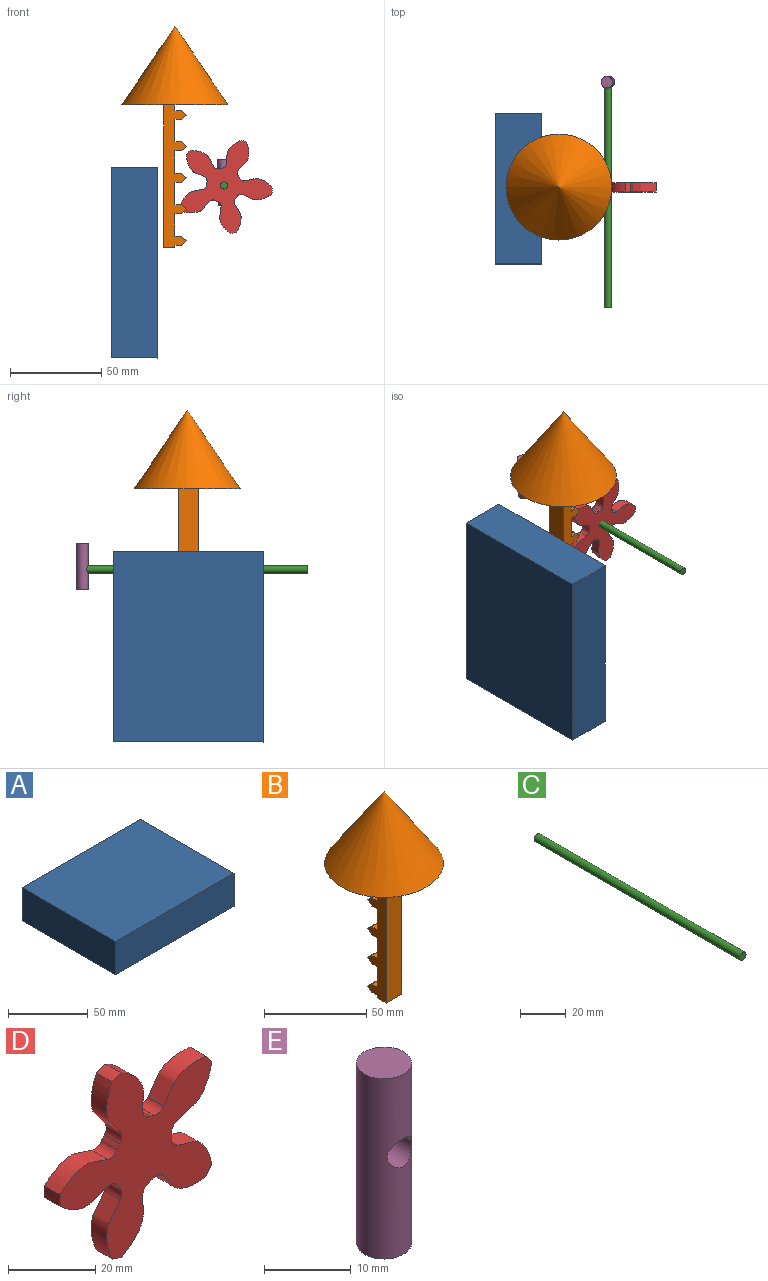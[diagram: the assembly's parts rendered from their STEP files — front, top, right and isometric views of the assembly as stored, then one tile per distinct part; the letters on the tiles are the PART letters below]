
ASSEMBLY  parts=5 mates=3
PART A: 6 faces, bbox 104.7x82.7x25.4 mm
  f0: plane 104.67x25.4mm, normal (0,1,0), area 2658.7mm2, adj f1,f3,f4,f5
  f1: plane 82.72x25.4mm, normal (-1,0,0), area 2101mm2, adj f0,f2,f4,f5
  f2: plane 104.67x25.4mm, normal (0,-1,0), area 2658.7mm2, adj f1,f3,f4,f5
  f3: plane 82.72x25.4mm, normal (1,0,0), area 2101mm2, adj f0,f2,f4,f5
  f4: plane 104.67x82.72mm, normal (0,0,1), area 8658.4mm2, adj f0,f1,f2,f3
  f5: plane 104.67x82.72mm, normal (0,0,-1), area 8658.4mm2, adj f0,f1,f2,f3
PART B: 32 faces, bbox 58.2x58.2x121.8 mm
  f0: plane 78.49x10.66mm, normal (0,-1,0), area 836.5mm2, adj f27,f28,f30,f31
  f1: plane 10.66x3.11mm, normal (0,1,0), area 33.1mm2, adj f26,f28,f30,f31
  f2: plane 10.66x1.43mm, normal (0,1,0), area 15.3mm2, adj f13,f27,f30,f31
  f3: plane 10.66x2.79mm, normal (0,0.64,-0.76), area 38.9mm2, adj f4,f13,f30,f31
  f4: plane 10.66x2.79mm, normal (0,0.67,0.74), area 39.9mm2, adj f3,f14,f30,f31
  f5: plane 10.66x2.79mm, normal (0,0.64,-0.76), area 38.9mm2, adj f6,f16,f30,f31
  f6: plane 10.66x2.79mm, normal (0,0.67,0.74), area 39.9mm2, adj f5,f17,f30,f31
  f7: plane 10.66x2.79mm, normal (0,0.64,-0.76), area 38.9mm2, adj f8,f19,f30,f31
  f8: plane 10.66x2.79mm, normal (0,0.67,0.74), area 39.9mm2, adj f7,f20,f30,f31
  f9: plane 10.66x2.79mm, normal (0,0.64,-0.76), area 38.9mm2, adj f10,f22,f30,f31
  f10: plane 10.66x2.79mm, normal (0,0.67,0.74), area 39.9mm2, adj f9,f23,f30,f31
  f11: plane 10.66x2.79mm, normal (0,0.64,-0.76), area 38.9mm2, adj f12,f25,f30,f31
  f12: plane 10.66x2.79mm, normal (0,0.67,0.74), area 39.9mm2, adj f11,f26,f30,f31
  f13: plane 10.66x3.77mm, normal (0,0,-1), area 40.2mm2, adj f2,f3,f30,f31
  f14: plane 10.66x3.77mm, normal (0,0,1), area 40.2mm2, adj f4,f15,f30,f31
  f15: plane 12.42x10.66mm, normal (0,1,0), area 132.3mm2, adj f14,f16,f30,f31
  f16: plane 10.66x3.77mm, normal (0,0,-1), area 40.2mm2, adj f5,f15,f30,f31
  f17: plane 10.66x3.77mm, normal (0,0,1), area 40.2mm2, adj f6,f18,f30,f31
  f18: plane 12.42x10.66mm, normal (0,1,0), area 132.3mm2, adj f17,f19,f30,f31
  f19: plane 10.66x3.77mm, normal (0,0,-1), area 40.2mm2, adj f7,f18,f30,f31
  f20: plane 10.66x3.77mm, normal (0,0,1), area 40.2mm2, adj f8,f21,f30,f31
  f21: plane 12.42x10.66mm, normal (0,1,0), area 132.3mm2, adj f20,f22,f30,f31
  f22: plane 10.66x3.77mm, normal (0,0,-1), area 40.2mm2, adj f9,f21,f30,f31
  f23: plane 10.66x3.77mm, normal (0,0,1), area 40.2mm2, adj f10,f24,f30,f31
  f24: plane 12.42x10.66mm, normal (0,1,0), area 132.3mm2, adj f23,f25,f30,f31
  f25: plane 10.66x3.77mm, normal (0,0,-1), area 40.2mm2, adj f11,f24,f30,f31
  f26: plane 10.66x3.77mm, normal (0,0,1), area 40.2mm2, adj f1,f12,f30,f31
  f27: plane 10.66x6.14mm, normal (0,0,-1), area 65.5mm2, adj f0,f2,f30,f31
  f28: plane 58.19x58.19mm, normal (0,0,-1), area 2594.1mm2, adj f0,f1,f29,f30,f31
  f29: cone r=29.1mm half-angle=33.9deg, axis (0,0,-1), area 4770.6mm2, adj f28
  f30: plane 78.49x12.7mm, normal (1,0,0), area 607.4mm2, adj f0,f1,f2,f3,f4,f5,f6,f7
  f31: plane 78.49x12.7mm, normal (-1,0,0), area 607.4mm2, adj f0,f1,f2,f3,f4,f5,f6,f7
PART C: 3 faces, bbox 4x127x4 mm
  f0: cylinder r=1.99mm len=127mm, axis (0,1,0), area 1585.8mm2, adj f1,f2
  f1: plane 3.97x3.97mm, normal (0,-1,0), area 12.4mm2, adj f0
  f2: plane 3.97x3.97mm, normal (0,1,0), area 12.4mm2, adj f0
PART D: 32 faces, bbox 49.5x5.1x52.1 mm
  f0: cylinder r=26.67mm len=5.08mm, axis (0,1,0), area 16.2mm2, adj f4,f6,f12,f29
  f1: cylinder r=26.67mm len=5.08mm, axis (0,1,0), area 16.2mm2, adj f4,f6,f24,f27
  f2: cylinder r=26.67mm len=5.08mm, axis (0,1,0), area 16.2mm2, adj f4,f6,f7,f19
  f3: cylinder r=26.67mm len=5.08mm, axis (0,1,0), area 16.2mm2, adj f4,f6,f14,f17
  f4: plane 52.12x49.47mm, normal (0,-1,0), area 1078.2mm2, adj f0,f1,f2,f3,f5,f7,f8,f9
  f5: cylinder r=26.67mm len=5.08mm, axis (0,1,0), area 16.2mm2, adj f4,f6,f9,f22
  f6: plane 52.12x49.47mm, normal (0,1,0), area 1078.2mm2, adj f0,f1,f2,f3,f5,f7,f8,f9
  f7: extruded ~11.11x10.86mm, area 85.6mm2, adj f2,f4,f6,f10
  f8: cylinder r=9.53mm len=5.08mm, axis (0,1,0), area 7.7mm2, adj f4,f6,f10,f11
  f9: extruded ~11.11x10.86mm, area 85.6mm2, adj f4,f5,f6,f11
  f10: cylinder r=2.65mm len=5.08mm, axis (0,1,0), area 18.2mm2, adj f4,f6,f7,f8
  f11: cylinder r=2.65mm len=5.08mm, axis (0,1,0), area 18.2mm2, adj f4,f6,f8,f9
  f12: extruded ~15.38x5.08mm, area 85.6mm2, adj f0,f4,f6,f15
  f13: cylinder r=9.53mm len=5.08mm, axis (0,1,0), area 7.7mm2, adj f4,f6,f15,f16
  f14: extruded ~15.32x5.08mm, area 85.6mm2, adj f3,f4,f6,f16
  f15: cylinder r=2.65mm len=5.08mm, axis (0,1,0), area 18.2mm2, adj f4,f6,f12,f13
  f16: cylinder r=2.65mm len=5.08mm, axis (0,1,0), area 18.2mm2, adj f4,f6,f13,f14
  f17: extruded ~13.93x6.98mm, area 85.6mm2, adj f3,f4,f6,f20
  f18: cylinder r=9.53mm len=5.08mm, axis (0,1,0), area 7.7mm2, adj f4,f6,f20,f21
  f19: extruded ~13.77x7.42mm, area 85.6mm2, adj f2,f4,f6,f21
  f20: cylinder r=2.65mm len=5.08mm, axis (0,1,0), area 18.2mm2, adj f4,f6,f17,f18
  f21: cylinder r=2.65mm len=5.08mm, axis (0,1,0), area 18.2mm2, adj f4,f6,f18,f19
  f22: extruded ~13.77x7.42mm, area 85.6mm2, adj f4,f5,f6,f25
  f23: cylinder r=9.53mm len=5.08mm, axis (0,1,0), area 7.7mm2, adj f4,f6,f25,f26
  f24: extruded ~13.93x6.98mm, area 85.6mm2, adj f1,f4,f6,f26
  f25: cylinder r=2.65mm len=5.08mm, axis (0,1,0), area 18.2mm2, adj f4,f6,f22,f23
  f26: cylinder r=2.65mm len=5.08mm, axis (0,1,0), area 18.2mm2, adj f4,f6,f23,f24
  f27: extruded ~15.32x5.08mm, area 85.6mm2, adj f1,f4,f6,f30
  f28: cylinder r=9.53mm len=5.08mm, axis (0,1,0), area 7.7mm2, adj f4,f6,f30,f31
  f29: extruded ~15.38x5.08mm, area 85.6mm2, adj f0,f4,f6,f31
  f30: cylinder r=2.65mm len=5.08mm, axis (0,1,0), area 18.2mm2, adj f4,f6,f27,f28
  f31: cylinder r=2.65mm len=5.08mm, axis (0,1,0), area 18.2mm2, adj f4,f6,f28,f29
PART E: 4 faces, bbox 6.4x6.4x25.4 mm
  f0: cylinder r=3.17mm len=25.4mm, axis (0,0,-1), area 480.5mm2, adj f1,f2,f3
  f1: plane 6.35x6.35mm, normal (0,0,1), area 31.7mm2, adj f0
  f2: plane 6.35x6.35mm, normal (0,0,-1), area 31.7mm2, adj f0
  f3: cylinder r=1.99mm len=6.35mm, axis (0,-1,0), area 70.8mm2, adj f0
PLACE A rot(axis=(0,-1,0),90deg) t=(18.31,-87.76,72.96)mm fixed
PLACE B rot(axis=(0,0,-1),90deg) t=(27.74,-81.08,157.11)mm
PLACE C rot(axis=(0,1,0),110deg) t=(41.16,-20.21,117.76)mm fixed
PLACE D rot(axis=(0,1,0),114.7deg) t=(54.65,-78.63,112.85)mm
PLACE E rot(axis=(0,1,0),177.7deg) t=(54.07,-23.43,127.2)mm
MATE revolute D.f0 <-> C.f0  axis (0,-1,0) through (54.65,-83.71,112.85)mm
MATE revolute C.f0 <-> E.f3  axis (0,1,0) through (54.65,-20.21,112.85)mm
MATE slider A.f3 <-> B.f27  axis (0,0,1) through (18.31,-81.74,122.74)mm
